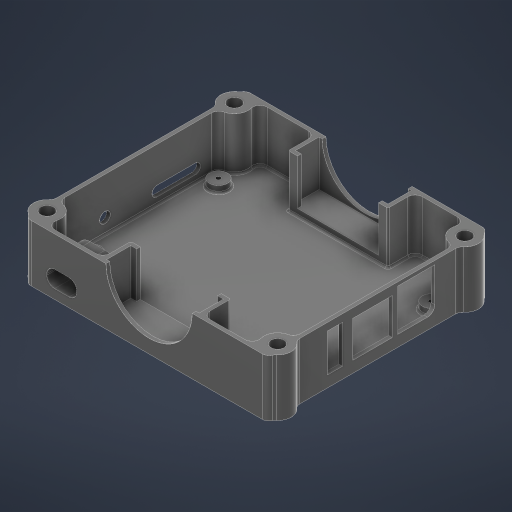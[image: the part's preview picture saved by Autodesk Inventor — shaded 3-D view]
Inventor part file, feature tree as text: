
AUTODESK INVENTOR PART (.ipt)
format: ipt  version: 2023 (Build 270158000, 158)  size: 849,920 bytes
history: native  units: in
note: dims shown in document units (in); Inventor stores cm internally (conversion verified against a paired STEP export)
features: reference x19, sketch x18, extrude x16, projected_geometry x5, other x4, plane x3, fillet x3, hole x2
ambient origin geometry x8: Origin, YZ Plane, XZ Plane, XY Plane, X Axis, Y Axis, Z Axis, Center Point
bodies: Solid1 (feature_tree)
feature tree (70):
  plane  "Work Plane1"
  extrude  "Extrusion1"  Depth=0.04in
  extrude  "Extrusion2"  Depth=0.5512in
  extrude  "Extrusion3"  Depth=0.065in
  extrude  "Extrusion4"  TaperAngle=0.0deg  [1 undecoded]
  extrude  "Extrusion5"  Depth=0.065in TaperAngle=0.0deg
  extrude  "Extrusion6"  Depth=0.0787in TaperAngle=0.0deg
  sketch  "Sketch7"  dims[d16=0.1in d17=0.1181in d18=0.0in]
  plane  "Work Plane2"
  extrude  "Extrusion7"  Depth=0.1181in TaperAngle=0.0deg
  extrude  "Extrusion8"  Depth=0.1181in TaperAngle=0.0deg
  extrude  "Extrusion9"  Depth=0.1181in
  sketch  "Sketch10"  dims[d29=0.05in d30=0.15in]
  plane  "Work Plane3"
  extrude  "Extrusion10"  Depth=0.15in
  extrude  "Extrusion11"  Depth=1.7323in
  extrude  "Extrusion12"  Depth=0.4843in
  hole  "Hole1"  [1 undecoded]
  extrude  "Extrusion13"  Depth=0.1in
  fillet  "Fillet1"  Radius=0.063in
  extrude  "Extrusion14"  Depth=0.063in
  fillet  "Fillet2"  Radius=0.063in
  hole  "Hole2"  [1 undecoded]
  fillet  "Fillet3"  Radius=0.4724in
  extrude  "Extrusion15"  Depth=0.8661in
  extrude  "Extrusion16"  Depth=0.0312in
  sketch  "Sketch1"  dims[d0=0.04in d1=0.04in]
  reference  "Reference1"
  reference  "Reference2"
  sketch  "Sketch2"  dims[d2=0.5512in d3=0.5512in]
  projected_geometry  "Projected Loop1"
  sketch  "Sketch3"  dims[d5=0.065in d6=0.065in]
  sketch  "Sketch4"  dims[d7=0.065in d8=0.0in]
  reference  "Reference3"
  reference  "Reference4"
  reference  "Reference5"
  reference  "Reference6"
  sketch  "Sketch5"  dims[d9=0.065in d10=0.7874in d11=0.0in]
  reference  "Reference7"
  reference  "Reference8"
  reference  "Reference9"
  sketch  "Sketch6"  dims[d12=0.1969in d13=0.0in d14=0.0787in d15=0.0in]
  reference  "Reference10"
  reference  "Reference11"
  sketch  "Sketch8"  dims[d19=0.6378in d22=0.1181in d23=0.0in]
  projected_geometry  "Projected Loop2"
  sketch  "Sketch9"  dims[d25=0.1181in d26=0.0in d28=1.7853in]
  sketch  "Sketch11"  dims[d31=0.05in d32=1.7323in]
  sketch  "Sketch12"  dims[d33=0.8661in d34=0.4843in]
  sketch  "Sketch13"  dims[d35=1.0in d36=0.0in d45=1.0in d46=0.0in]
  sketch  "Sketch14"  dims[d47=0.1in d48=0.1in d49=0.063in]
  projected_geometry  "Projected Loop3"
  projected_geometry  "Projected Loop4"
  sketch  "Sketch15"  dims[d50=0.063in d51=0.063in d52=0.063in]
  sketch  "Sketch17"  dims[d53=1.4961in d54=1.0in d55=0.0in d56=0.4724in]
  sketch  "Sketch18"  dims[d57=1.7323in d58=0.8661in]
  projected_geometry  "Projected Loop5"
  sketch  "Sketch19"  dims[d59=1.0in d60=0.0in d62=0.063in d63=0.1in d64=0.063in d65=0.063in d66=0.063in d67=0.1in d68=1.0in d69=0.0in d70=1.4961in d71=1.0in d72=0.0in d73=0.0793in d74=0.197in d75=0.173in d76=0.079in d77=0.5635in d78=1.0in d79=0.8108in d81=0.625in d82=0.0in d83=0.125in d84=3.25in d85=4.0in d86=0.4724in d87=0.1969in d88=0.0in d89=0.125in d90=0.2283in d91=0.75in d92=0.3125in d93=0.164in d94=0.5635in d95=1.0in d96=0.8108in d97=0.0312in d98=1.0in d99=0.0in d102=0.1875in d103=1.0in d104=0.0in d105=0.025in d106=0.1in d100=0.0in d101=0.0in]
  reference  "Reference12"
  reference  "Reference13"
  reference  "Reference14"
  reference  "Reference15"
  reference  "Reference16"
  reference  "Reference17"
  reference  "Reference18"
  reference  "Reference19"
  other  "OrangePICover.iam"
  other  "OPi5_pcb_asm-0809:1"
  other  "orangepicover-001a:1"
  other  "Assembly10"
note: 3 required parameter values undecoded (feature->parameter linkage not recoverable at this tier; creation-order binding heuristic only, values carry confidence <= 0.55)
